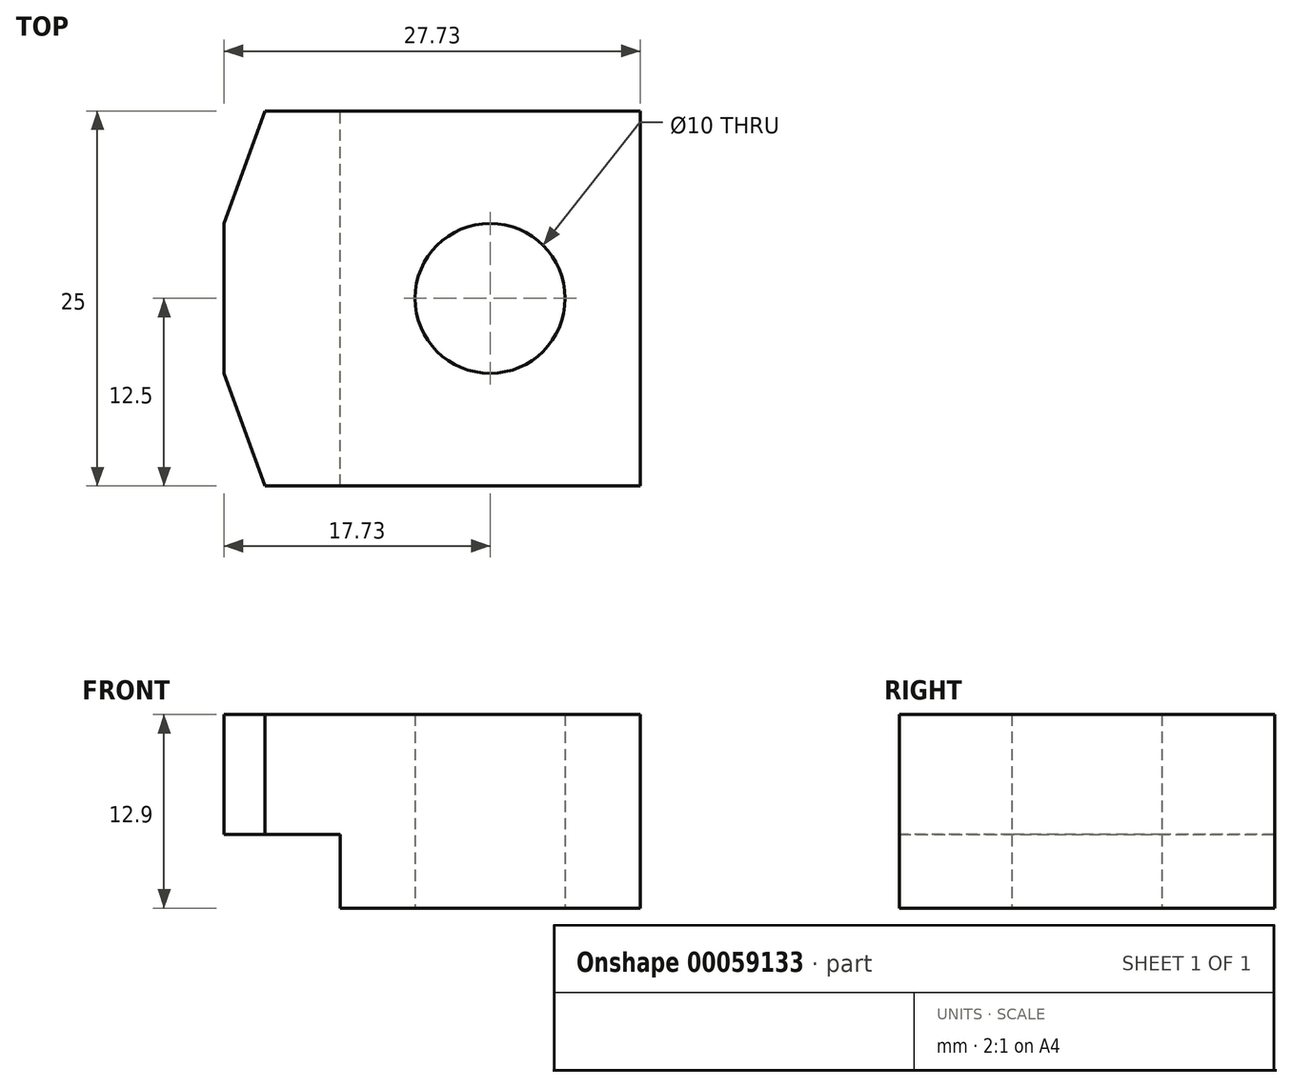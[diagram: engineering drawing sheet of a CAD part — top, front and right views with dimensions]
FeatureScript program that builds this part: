
annotation { "Feature Type Name" : "Feature", "Feature Type Description" : "" }
export const myFeature = defineFeature(function(context is Context, id is Id, definition is map)
    precondition{}
    {
        {
            var Q0;
            Q0=qCreatedBy(makeId("Top.planeOp"),FACE);
            var sketch = newSketch(context, id + "F0", { "sketchPlane" : qUnion([Q0])});
            skLineSegment(sketch, "E0.bottom", {"start": v(0, 36.5) * mm, "end": v(-190, 36.5) * mm, "construction": true});
            skLineSegment(sketch, "E0.top", {"start": v(0, -36.5) * mm, "end": v(-190, -36.5) * mm, "construction": true});
            skLineSegment(sketch, "E0.right", {"start": v(-190, 36.5) * mm, "end": v(-190, -36.5) * mm, "construction": true});
            skArc(sketch, "E1", {"start": v(0, 31.5) * mm, "mid": v(-10, 0) * mm, "end": v(0, -31.5) * mm, "construction": true});
            skCircle(sketch, "E2", {"center": v(10, 0) * mm, "radius": 5 * mm});
            skLineSegment(sketch, "E3", {"start": v(20, -12.5) * mm, "end": v(-5, -12.5) * mm});
            skLineSegment(sketch, "E4", {"start": v(-5, 12.5) * mm, "end": v(20, 12.5) * mm});
            skLineSegment(sketch, "E5", {"start": v(20, 12.5) * mm, "end": v(20, -12.5) * mm});
            skLineSegment(sketch, "E6", {"start": v(20, 0) * mm, "end": v(-16.32, 0) * mm, "construction": true});
            skLineSegment(sketch, "E7", {"start": v(-5, 12.5) * mm, "end": v(-7.73, 5) * mm});
            skLineSegment(sketch, "E8", {"start": v(-7.73, -5) * mm, "end": v(-5, -12.5) * mm});
            skLineSegment(sketch, "E9", {"start": v(-7.73, 5) * mm, "end": v(-7.73, -5) * mm});
            skLineSegment(sketch, "E10", {"start": v(0, 36.5) * mm, "end": v(0, -36.5) * mm, "construction": true});
            skSolve(sketch);
        }
        {
            var Q0;
            Q0=qSketchRegion(id+"F0",true);
            extrude(context, id + "F1", {"entities" : qUnion([Q0]), "depth" : 8 * mm});
        }
        {
            var Q0;
            Q0=qCreatedBy(makeId("Top.planeOp"),FACE);
            var sketch = newSketch(context, id + "F2", { "sketchPlane" : qUnion([Q0])});
            skLineSegment(sketch, "E11.0", {"start": v(20, -12.5) * mm, "end": v(0, -12.5) * mm});
            skLineSegment(sketch, "E11.1", {"start": v(20, 12.5) * mm, "end": v(20, -12.5) * mm});
            skLineSegment(sketch, "E11.2", {"start": v(0, 12.5) * mm, "end": v(20, 12.5) * mm});
            skCircle(sketch, "E12.0", {"center": v(10, 0) * mm, "radius": 5 * mm});
            skLineSegment(sketch, "E13", {"start": v(0, -12.5) * mm, "end": v(0, 12.5) * mm});
            skSolve(sketch);
        }
        {
            var Q0;
            Q0=makeQuery(id+"F2.imprint","IMPRINT",FACE,{"disambiguationData":[TD([[makeQuery(id+"F2.imprint","IMPRINT",EDGE,{"derivedFrom":sQuery(id+"F2.wireOp",EDGE,"E11.0")}),-1.0]])]});
            extrude(context, id + "F3", {"entities" : qUnion([Q0]), "operationType" : NewBodyOperationType.ADD, "oppositeDirection" : true, "depth" : 4.9 * mm});
        }
    });
